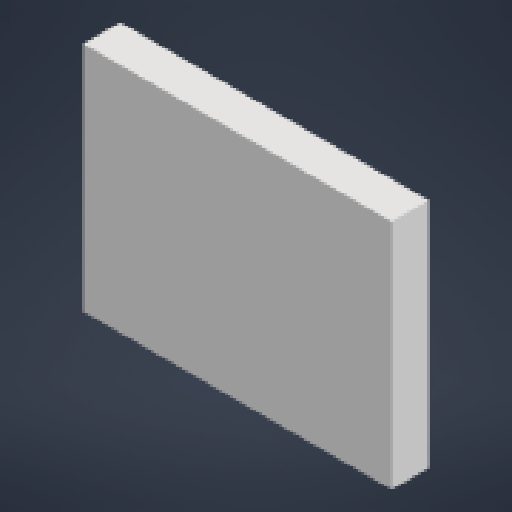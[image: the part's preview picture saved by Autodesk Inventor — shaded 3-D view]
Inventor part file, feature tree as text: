
AUTODESK INVENTOR PART (.ipt)
format: ipt  version: 2025.2 (Build 292293000, 293)  size: 117,760 bytes
history: native  units: in
note: dims shown in document units (in); Inventor stores cm internally (conversion verified against a paired STEP export)
features: reference x11, other x5, extrude x1, sketch x1
ambient origin geometry x8: Origin, YZ Plane, XZ Plane, XY Plane, X Axis, Y Axis, Z Axis, Center Point
bodies: Solid1 (feature_tree)
feature tree (18):
  extrude  "Extrusion1"  [1 undecoded]
  sketch  "Sketch1"  dims[d0=0.7874in d1=0.0in]
  reference  "Reference1"
  reference  "Reference2"
  reference  "Reference3"
  reference  "Reference4"
  reference  "Reference5"
  reference  "Reference6"
  reference  "Reference7"
  reference  "Reference8"
  reference  "Reference9"
  reference  "Reference10"
  reference  "Reference11"
  other  "18650ASSEMBLYfordrawing.iam"
  other  "cooling plate:2"
  other  "PILLARSCELLCASE18650:2"
  other  "insulation:1"
  other  "insulation:2"
note: 1 required parameter value undecoded (feature->parameter linkage not recoverable at this tier; creation-order binding heuristic only, values carry confidence <= 0.55)
